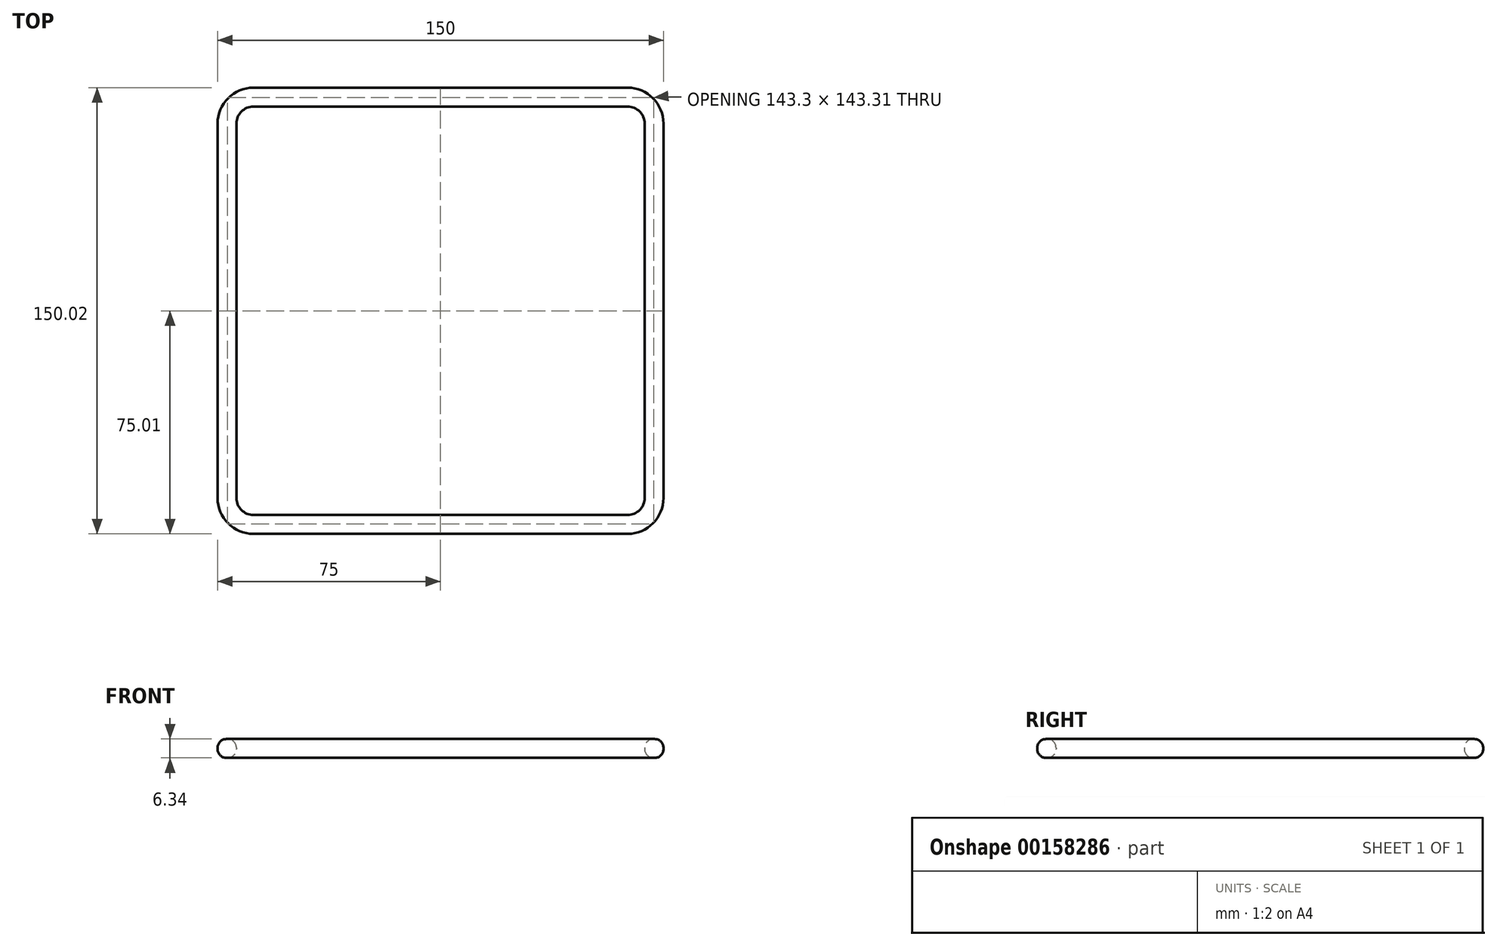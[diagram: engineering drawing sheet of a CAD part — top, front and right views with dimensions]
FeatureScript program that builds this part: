
annotation { "Feature Type Name" : "Feature", "Feature Type Description" : "" }
export const myFeature = defineFeature(function(context is Context, id is Id, definition is map)
    precondition{}
    {
        {
            var Q0;
            Q0=qCreatedBy(makeId("Top.planeOp"),FACE);
            var sketch = newSketch(context, id + "F0", { "sketchPlane" : qUnion([Q0])});
            skLineSegment(sketch, "E0.bottom", {"start": v(-62.93, 75) * mm, "end": v(62.93, 75) * mm});
            skLineSegment(sketch, "E0.top", {"start": v(-62.93, -75) * mm, "end": v(62.93, -75) * mm});
            skLineSegment(sketch, "E0.left", {"start": v(-75, 62.94) * mm, "end": v(-75, -62.94) * mm});
            skLineSegment(sketch, "E0.right", {"start": v(75, 62.94) * mm, "end": v(75, -62.94) * mm});
            skPoint(sketch, "E0.middle", {"position": v(0, 0) * mm});
            skPoint(sketch, "E1.visualSharp", {"position": v(-75, 75) * mm});
            skArc(sketch, "E1.filletArc", {"start": v(-62.93, 75) * mm, "mid": v(-71.46, 71.47) * mm, "end": v(-75, 62.94) * mm});
            skPoint(sketch, "E2.visualSharp", {"position": v(-75, -75) * mm});
            skArc(sketch, "E2.filletArc", {"start": v(-75, -62.94) * mm, "mid": v(-71.46, -71.47) * mm, "end": v(-62.93, -75) * mm});
            skPoint(sketch, "E3.visualSharp", {"position": v(75, -75) * mm});
            skArc(sketch, "E3.filletArc", {"start": v(62.93, -75) * mm, "mid": v(71.46, -71.47) * mm, "end": v(75, -62.94) * mm});
            skPoint(sketch, "E4.visualSharp", {"position": v(75, 75) * mm});
            skArc(sketch, "E4.filletArc", {"start": v(75, 62.94) * mm, "mid": v(71.46, 71.47) * mm, "end": v(62.93, 75) * mm});
            skArc(sketch, "E5.0", {"start": v(-62.93, 68.66) * mm, "mid": v(-66.97, 66.98) * mm, "end": v(-68.65, 62.94) * mm});
            skLineSegment(sketch, "E5.1", {"start": v(-68.65, 62.94) * mm, "end": v(-68.65, -62.94) * mm});
            skLineSegment(sketch, "E5.2", {"start": v(-62.93, 68.66) * mm, "end": v(62.93, 68.66) * mm});
            skArc(sketch, "E5.3", {"start": v(-68.65, -62.94) * mm, "mid": v(-66.97, -66.98) * mm, "end": v(-62.93, -68.66) * mm});
            skArc(sketch, "E5.4", {"start": v(68.65, 62.94) * mm, "mid": v(66.97, 66.98) * mm, "end": v(62.93, 68.66) * mm});
            skLineSegment(sketch, "E5.5", {"start": v(68.65, 62.94) * mm, "end": v(68.65, -62.94) * mm});
            skArc(sketch, "E5.6", {"start": v(62.93, -68.66) * mm, "mid": v(66.97, -66.98) * mm, "end": v(68.65, -62.94) * mm});
            skLineSegment(sketch, "E5.7", {"start": v(-62.93, -68.66) * mm, "end": v(62.93, -68.66) * mm});
            skSolve(sketch);
        }
        {
            var Q0;
            Q0 = qSketchRegion(id + "F0", true);
            extrude(context, id + "F1", {"entities" : qUnion([Q0]), "endBound" : BoundingType.SYMMETRIC, "depth" : 6.35 * mm});
        }
        {
            var Q0;
            Q0=makeQuery(id+"F1.opExtrude","CAP_EDGE",EDGE,{"disambiguationData":[OSD([sQuery(id+"F0.wireOp",EDGE,"E0.top")])],"isStart":false});
            var Q1;
            Q1=makeQuery(id+"F1.opExtrude","CAP_EDGE",EDGE,{"disambiguationData":[OSD([sQuery(id+"F0.wireOp",EDGE,"E2.filletArc")])],"isStart":false});
            var Q2;
            Q2=makeQuery(id+"F1.opExtrude","CAP_EDGE",EDGE,{"disambiguationData":[OSD([sQuery(id+"F0.wireOp",EDGE,"E0.left")])],"isStart":false});
            var Q3;
            Q3=makeQuery(id+"F1.opExtrude","CAP_EDGE",EDGE,{"disambiguationData":[OSD([sQuery(id+"F0.wireOp",EDGE,"E1.filletArc")])],"isStart":false});
            var Q4;
            Q4=makeQuery(id+"F1.opExtrude","CAP_EDGE",EDGE,{"disambiguationData":[OSD([sQuery(id+"F0.wireOp",EDGE,"E0.bottom")])],"isStart":false});
            var Q5;
            Q5=makeQuery(id+"F1.opExtrude","CAP_EDGE",EDGE,{"disambiguationData":[OSD([sQuery(id+"F0.wireOp",EDGE,"E4.filletArc")])],"isStart":false});
            var Q6;
            Q6=makeQuery(id+"F1.opExtrude","CAP_EDGE",EDGE,{"disambiguationData":[OSD([sQuery(id+"F0.wireOp",EDGE,"E0.right")])],"isStart":false});
            var Q7;
            Q7=makeQuery(id+"F1.opExtrude","CAP_EDGE",EDGE,{"disambiguationData":[OSD([sQuery(id+"F0.wireOp",EDGE,"E3.filletArc")])],"isStart":false});
            var Q8;
            Q8=makeQuery(id+"F1.opExtrude","CAP_EDGE",EDGE,{"disambiguationData":[OSD([sQuery(id+"F0.wireOp",EDGE,"E0.right")])],"isStart":true});
            var Q9;
            Q9=makeQuery(id+"F1.opExtrude","CAP_EDGE",EDGE,{"disambiguationData":[OSD([sQuery(id+"F0.wireOp",EDGE,"E3.filletArc")])],"isStart":true});
            var Q10;
            Q10=makeQuery(id+"F1.opExtrude","CAP_EDGE",EDGE,{"disambiguationData":[OSD([sQuery(id+"F0.wireOp",EDGE,"E5.2")])],"isStart":true});
            var Q11;
            Q11=makeQuery(id+"F1.opExtrude","CAP_EDGE",EDGE,{"disambiguationData":[OSD([sQuery(id+"F0.wireOp",EDGE,"E5.2")])],"isStart":false});
            var Q12;
            Q12=makeQuery(id+"F1.opExtrude","CAP_EDGE",EDGE,{"disambiguationData":[OSD([sQuery(id+"F0.wireOp",EDGE,"E5.0")])],"isStart":true});
            var Q13;
            Q13=makeQuery(id+"F1.opExtrude","CAP_EDGE",EDGE,{"disambiguationData":[OSD([sQuery(id+"F0.wireOp",EDGE,"E5.1")])],"isStart":true});
            var Q14;
            Q14=makeQuery(id+"F1.opExtrude","CAP_EDGE",EDGE,{"disambiguationData":[OSD([sQuery(id+"F0.wireOp",EDGE,"E5.3")])],"isStart":true});
            var Q15;
            Q15=makeQuery(id+"F1.opExtrude","CAP_EDGE",EDGE,{"disambiguationData":[OSD([sQuery(id+"F0.wireOp",EDGE,"E5.7")])],"isStart":true});
            var Q16;
            Q16=makeQuery(id+"F1.opExtrude","CAP_EDGE",EDGE,{"disambiguationData":[OSD([sQuery(id+"F0.wireOp",EDGE,"E5.6")])],"isStart":true});
            var Q17;
            Q17=makeQuery(id+"F1.opExtrude","CAP_EDGE",EDGE,{"disambiguationData":[OSD([sQuery(id+"F0.wireOp",EDGE,"E5.5")])],"isStart":true});
            var Q18;
            Q18=makeQuery(id+"F1.opExtrude","CAP_EDGE",EDGE,{"disambiguationData":[OSD([sQuery(id+"F0.wireOp",EDGE,"E5.4")])],"isStart":true});
            fillet(context, id + "F2", {"entities" : qUnion([Q0, Q1, Q2, Q3, Q4, Q5, Q6, Q7, Q8, Q9, Q10, Q11, Q12, Q13, Q14, Q15, Q16, Q17, Q18]), "radius" : 3 * mm, "tangentPropagation" : true, "allowEdgeOverflow" : false});
        }
    });
